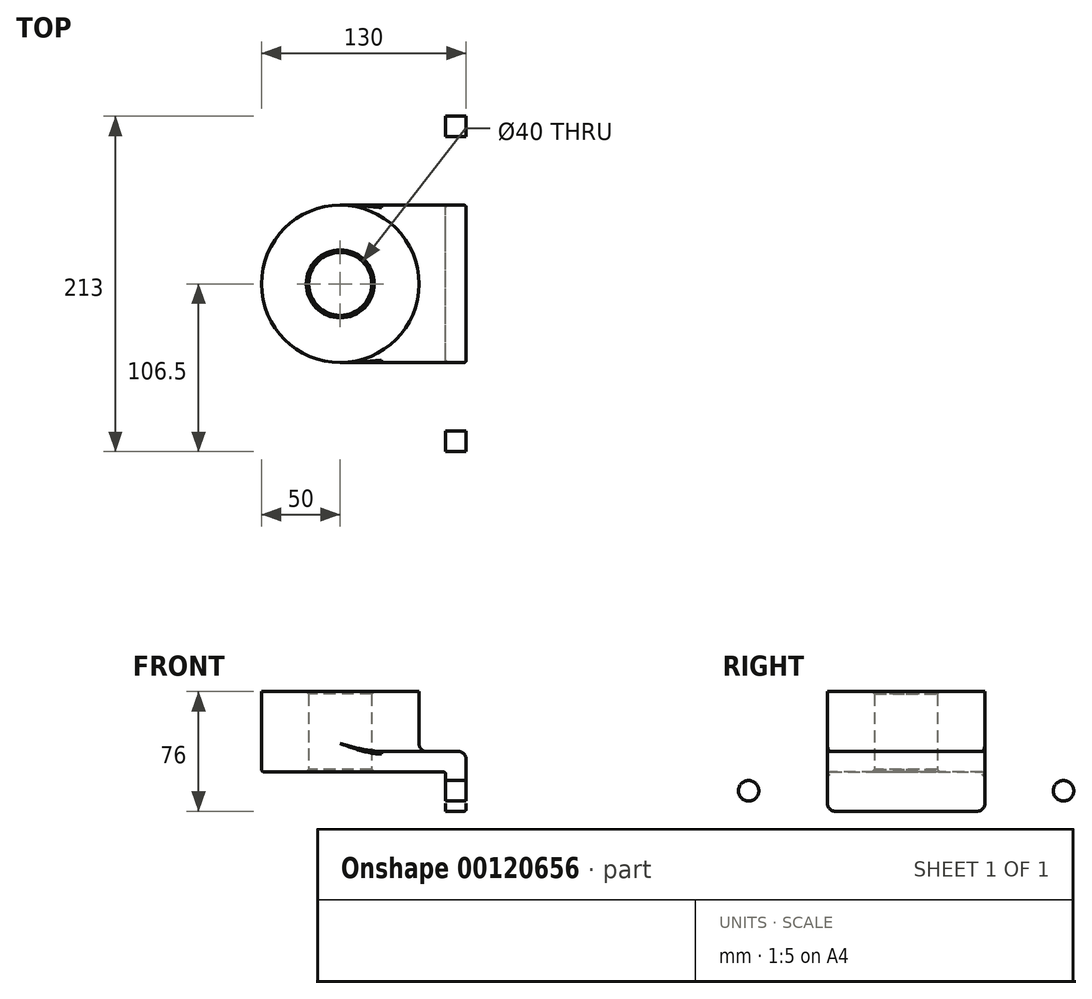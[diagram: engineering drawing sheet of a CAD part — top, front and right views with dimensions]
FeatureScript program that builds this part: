
annotation { "Feature Type Name" : "Feature", "Feature Type Description" : "" }
export const myFeature = defineFeature(function(context is Context, id is Id, definition is map)
    precondition{}
    {
        {
            var Q0;
            Q0=qCreatedBy(makeId("Top.planeOp"),FACE);
            var sketch = newSketch(context, id + "F0", { "sketchPlane" : qUnion([Q0])});
            skLineSegment(sketch, "E0.bottom", {"start": v(-40, 50) * mm, "end": v(40, 50) * mm});
            skLineSegment(sketch, "E0.top", {"start": v(-40, -50) * mm, "end": v(40, -50) * mm});
            skLineSegment(sketch, "E0.left", {"start": v(-40, 50) * mm, "end": v(-40, -50) * mm});
            skLineSegment(sketch, "E0.right", {"start": v(40, 50) * mm, "end": v(40, -50) * mm});
            skPoint(sketch, "E0.middle", {"position": v(0, 0) * mm});
            skCircle(sketch, "E1", {"center": v(-40, 0) * mm, "radius": 50 * mm});
            skCircle(sketch, "E2", {"center": v(-40, 0) * mm, "radius": 20 * mm});
            skSolve(sketch);
        }
        {
            var Q0;
            Q0 = qSketchRegion(id + "F0", true);
            extrude(context, id + "F1", {"entities" : qUnion([Q0]), "depth" : 13 * mm});
        }
        {
            var Q0;
            {var subQ1=sQuery(id+"F0.wireOp",EDGE,"E0.left");var subQ3=sQuery(id+"F0.wireOp",EDGE,"E2");var subQ4=makeQuery(id+"F0.imprint","INTERSECT",VERTEX,{"disambiguationData":[OD(0.0)],"derivedFrom":[subQ1,subQ3]});Q0=makeQuery(id+"F0.imprint","IMPRINT",FACE,{"disambiguationData":[TD([[makeQuery(id+"F0.imprint","IMPRINT",EDGE,{"disambiguationData":[TD([[subQ4,-1.0]])],"derivedFrom":subQ3}),-1.0]])]});}
            var Q1;
            {var subQ1=sQuery(id+"F0.wireOp",EDGE,"E0.left");var subQ3=sQuery(id+"F0.wireOp",EDGE,"E2");var subQ4=makeQuery(id+"F0.imprint","INTERSECT",VERTEX,{"disambiguationData":[OD(0.0)],"derivedFrom":[subQ1,subQ3]});Q1=makeQuery(id+"F0.imprint","IMPRINT",FACE,{"disambiguationData":[TD([[makeQuery(id+"F0.imprint","IMPRINT",EDGE,{"disambiguationData":[TD([[subQ4,1.0]])],"derivedFrom":subQ3}),-1.0]])]});}
            extrude(context, id + "F2", {"entities" : qUnion([Q0, Q1]), "operationType" : NewBodyOperationType.ADD, "depth" : 51 * mm});
        }
        {
            var Q0;
            Q0=makeQuery(id+"F1.opExtrude","SWEPT_FACE",FACE,{"disambiguationData":[OSD([sQuery(id+"F0.wireOp",EDGE,"E0.right")])]});
            var sketch = newSketch(context, id + "F3", { "sketchPlane" : qUnion([Q0])});
            skLineSegment(sketch, "E3.bottom", {"start": v(-50, 13) * mm, "end": v(50, 13) * mm});
            skLineSegment(sketch, "E3.top", {"start": v(-50, -25) * mm, "end": v(50, -25) * mm});
            skLineSegment(sketch, "E3.left", {"start": v(-50, 13) * mm, "end": v(-50, -25) * mm});
            skLineSegment(sketch, "E3.right", {"start": v(50, 13) * mm, "end": v(50, -25) * mm});
            skCircle(sketch, "E4", {"center": v(-100, -12) * mm, "radius": 6.5 * mm});
            skLineSegment(sketch, "E5", {"start": v(0, 0) * mm, "end": v(0, -25) * mm, "construction": true});
            skCircle(sketch, "E6.MirrorC", {"center": v(100, -12) * mm, "radius": 6.5 * mm});
            skSolve(sketch);
        }
        {
            var Q0;
            Q0 = qSketchRegion(id + "F3", true);
            extrude(context, id + "F4", {"entities" : qUnion([Q0]), "operationType" : NewBodyOperationType.ADD, "oppositeDirection" : true, "depth" : 13 * mm});
        }
        {
            var Q0;
            {var subQ0=sQuery(id+"F0.wireOp",EDGE,"E1");Q0=makeQuery(id+"F2.boolean.opBoolean","INTERSECT",EDGE,{"derivedFrom":[makeQuery(id+"F1.opExtrude","CAP_FACE",FACE,{"disambiguationData":[OSD([sQuery(id+"F0.wireOp",EDGE,"E0.bottom"),sQuery(id+"F0.wireOp",EDGE,"E0.top"),sQuery(id+"F0.wireOp",EDGE,"E0.right"),subQ0,sQuery(id+"F0.wireOp",EDGE,"E2")])],"isStart":false}),makeQuery(id+"F2.opExtrude","SWEPT_FACE",FACE,{"disambiguationData":[OSD([subQ0])]})]});}
            var Q1;
            Q1=makeQuery(id+"F1.opExtrude","CAP_EDGE",EDGE,{"disambiguationData":[OSD([sQuery(id+"F0.wireOp",EDGE,"E0.right")])],"isStart":false});
            var Q2;
            Q2=makeQuery(id+"F4.opExtrude","SWEPT_EDGE",EDGE,{"disambiguationData":[OSD([sQuery(id+"F3.wireOp",EDGE,"E3.top"),sQuery(id+"F3.wireOp",EDGE,"E3.left")])]});
            var Q3;
            Q3=makeQuery(id+"F4.opExtrude","SWEPT_EDGE",EDGE,{"disambiguationData":[OSD([sQuery(id+"F3.wireOp",EDGE,"E3.top"),sQuery(id+"F3.wireOp",EDGE,"E3.right")])]});
            fillet(context, id + "F5", {"entities" : qUnion([Q0, Q1, Q2, Q3]), "radius" : 5 * mm, "tangentPropagation" : true, "allowEdgeOverflow" : false});
        }
        {
            var Q0;
            Q0=makeQuery(id+"F1.opExtrude","CAP_EDGE",EDGE,{"disambiguationData":[OSD([sQuery(id+"F0.wireOp",EDGE,"E0.top")])],"isStart":false});
            var Q1;
            Q1=makeQuery(id+"F1.opExtrude","CAP_EDGE",EDGE,{"disambiguationData":[OSD([sQuery(id+"F0.wireOp",EDGE,"E0.top")])],"isStart":true});
            var Q2;
            Q2=makeQuery(id+"F4.boolean.opBoolean","INTERSECT",EDGE,{"derivedFrom":[makeQuery(id+"F1.opExtrude","CAP_FACE",FACE,{"disambiguationData":[OSD([sQuery(id+"F0.wireOp",EDGE,"E0.bottom"),sQuery(id+"F0.wireOp",EDGE,"E0.top"),sQuery(id+"F0.wireOp",EDGE,"E0.right"),sQuery(id+"F0.wireOp",EDGE,"E1"),sQuery(id+"F0.wireOp",EDGE,"E2")])],"isStart":true}),makeQuery(id+"F4.opExtrude","CAP_FACE",FACE,{"disambiguationData":[OSD([sQuery(id+"F3.wireOp",EDGE,"E3.bottom"),sQuery(id+"F3.wireOp",EDGE,"E3.top"),sQuery(id+"F3.wireOp",EDGE,"E3.left"),sQuery(id+"F3.wireOp",EDGE,"E3.right"),sQuery(id+"F3.wireOp",EDGE,"E4"),sQuery(id+"F3.wireOp",EDGE,"E6.MirrorC")])],"isStart":false})]});
            var Q3;
            Q3=makeQuery(id+"F1.opExtrude","CAP_EDGE",EDGE,{"disambiguationData":[OSD([sQuery(id+"F0.wireOp",EDGE,"E0.bottom")])],"isStart":false});
            var Q4;
            Q4=makeQuery(id+"F1.opExtrude","CAP_EDGE",EDGE,{"disambiguationData":[OSD([sQuery(id+"F0.wireOp",EDGE,"E0.bottom")])],"isStart":true});
            fillet(context, id + "F6", {"entities" : qUnion([Q0, Q1, Q2, Q3, Q4]), "radius" : 1.6 * mm, "tangentPropagation" : true, "allowEdgeOverflow" : false});
        }
        {
            var Q0;
            {var subQ0=sQuery(id+"F0.wireOp",EDGE,"E2");Q0=makeQuery(id+"F2.boolean.opBoolean","MERGE",FACE,{"derivedFrom":[makeQuery(id+"F1.opExtrude","SWEPT_FACE",FACE,{"disambiguationData":[OSD([subQ0])]}),makeQuery(id+"F2.opExtrude","SWEPT_FACE",FACE,{"disambiguationData":[OSD([subQ0])]})]});}
            chamfer(context, id + "F7", {"entities" : qUnion([Q0]), "width" : 1.6 * mm, "tangentPropagation" : true});
        }
    });
